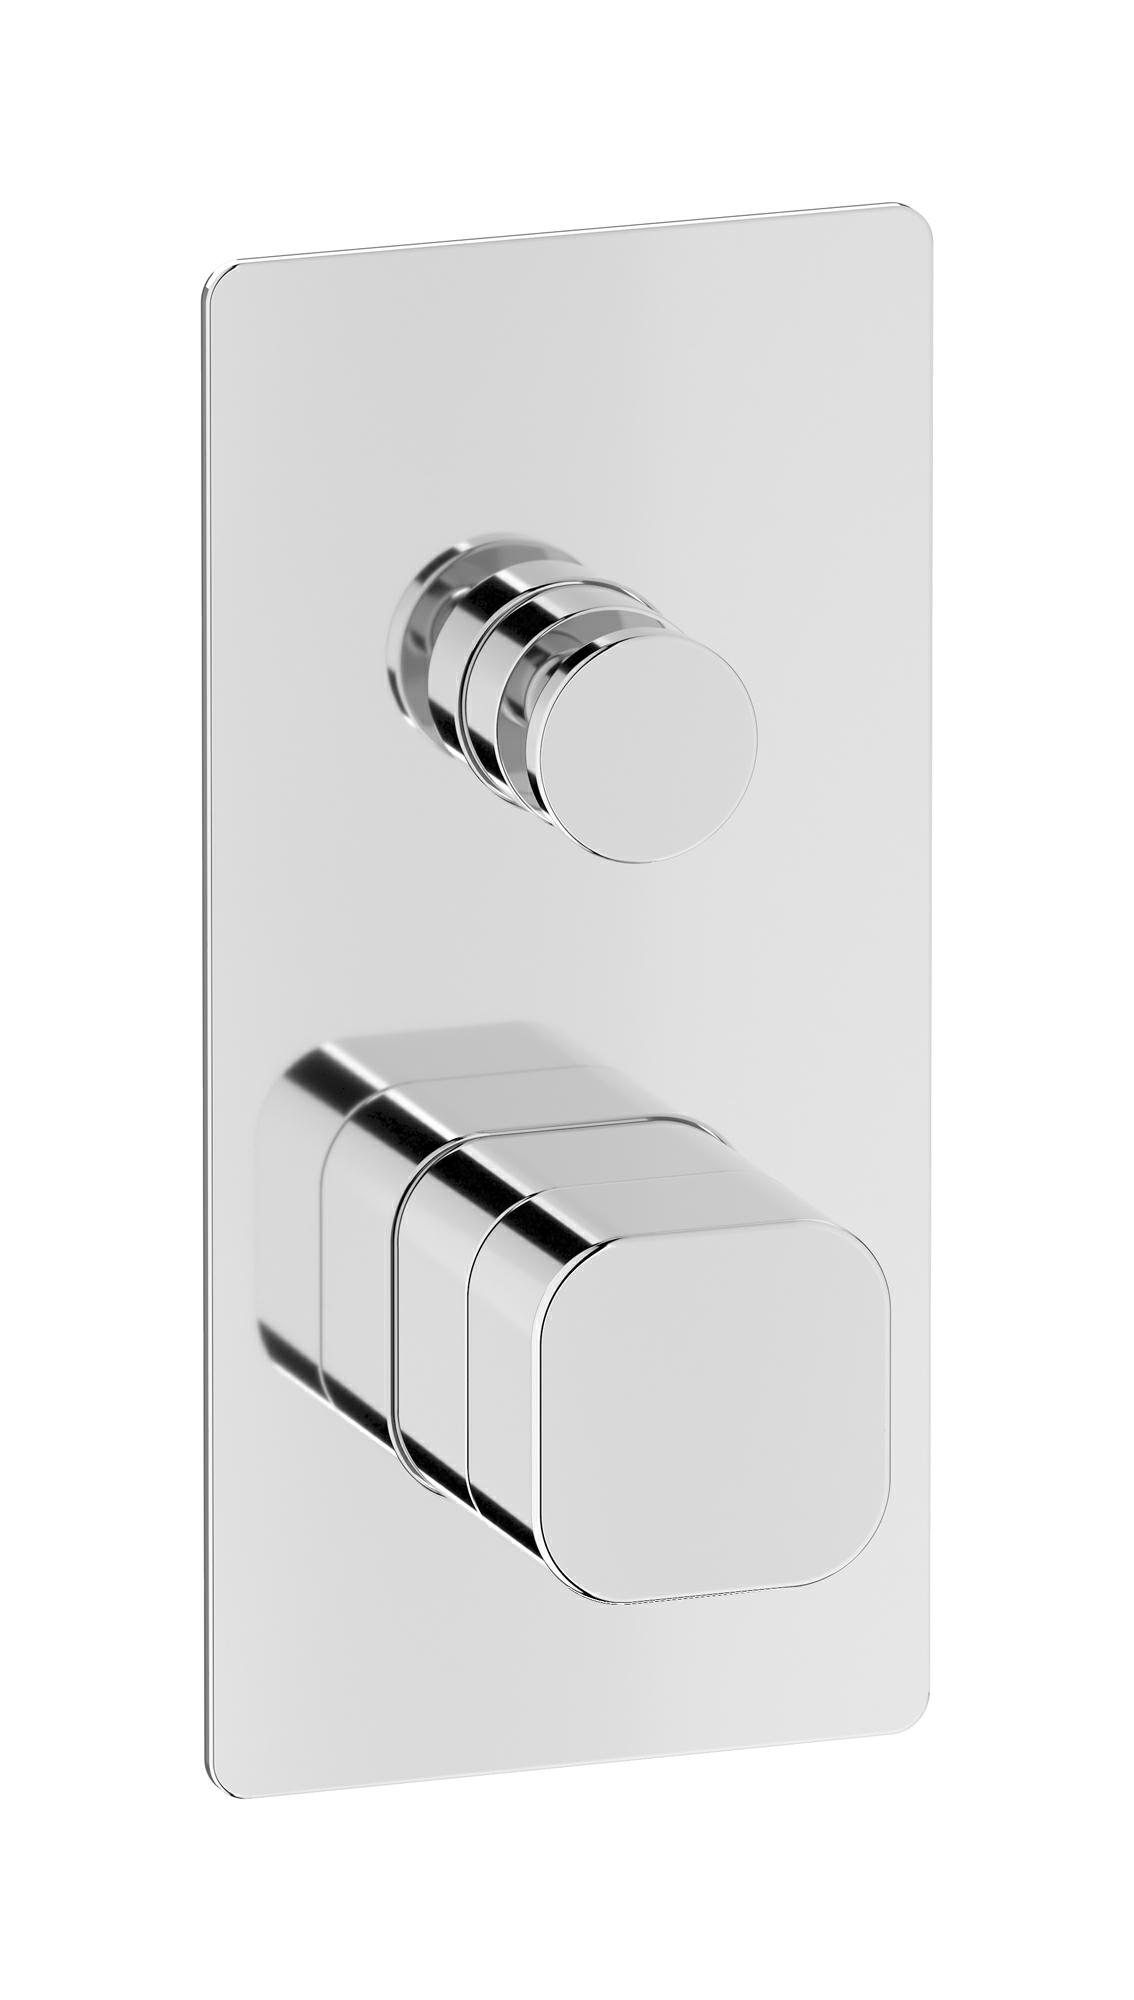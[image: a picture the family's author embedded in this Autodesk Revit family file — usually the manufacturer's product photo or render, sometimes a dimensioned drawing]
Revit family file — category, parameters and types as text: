
# Revit family: EO310_1
name_source: partatom
category: Apparecchi idraulici
units: mm (PartAtom-declared; Revit-internal decimal feet)

## family parameters
Basato su piano di lavoro = No
Condiviso = No
Mantieni orientamento annotazione = No
Numero OmniClass = 23.45.55.17
Punto di calcolo locali = No
Quota connettore circolare = Usa diametro
Sempre verticale = Sì
Taglio con vuoti quando caricato = No
Tipo di parte = Normale
Titolo OmniClass = Mixing Faucets

## types (12) — shared parameters
Cold water inlet = -10 mm  [stored -0.0328084 ft]
Commenti sul tipo = Shower mixer
Connessione CW = No
Connessione HW = No
Connessione di scarico = No
Connessione di ventilazione = No
Descrizione = Two ways shower mixer
Hot water inlet = -10 mm  [stored -0.0328084 ft]
Produttore = IB Rubinetterie S.p.A.
URL = https://www.weareib.it
zero-valued in all types: Prospetto di default

## per-type parameters (varying)
| type | Finishes surface | Immagine tipo | Modello |
| Chrome | IB_Chrome | EO310CC_1.jpg | EO310CC_1 |
| Brushed nickel | IB_Brushed nickel | EO310SS_1.jpg | EO310SS_1 |
| Natural brass | IB_Brass | EO310ON_1.jpg | EO310ON_1 |
| Matt black | IB_matt black | EO310NP_1.jpg | EO310NP_1 |
| Black chrome | IB_Black chrome | EO310CF_1.jpg | EO310CF_1 |
| Brushed black chrome | IB_Brushed black chrome | EO310CS_1.jpg | EO310CS_1 |
| Pale gold | IB_Pale gold | EO310II_1.jpg | EO310II_1 |
| Brushed pale gold | IB_brushed pale gold | EO310IS_1.jpg | EO310IS_1 |
| Rose gold | IB_Rose gold | EO310RS_1.jpg | EO310RS_1 |
| Brushed rose gold | IB_Brushed rose gold | EO310SR_1.jpg | EO310SR_1 |
| Gold | IB_gold | EO310OO_1.jpg | EO310OO_1 |
| Brushed gold | IB_brushed gold | EO310OS_1.jpg | EO310OS_1 |

note: [stored X ft] marks values corroborated as IEEE doubles in the binary element streams (Revit-internal decimal feet)
